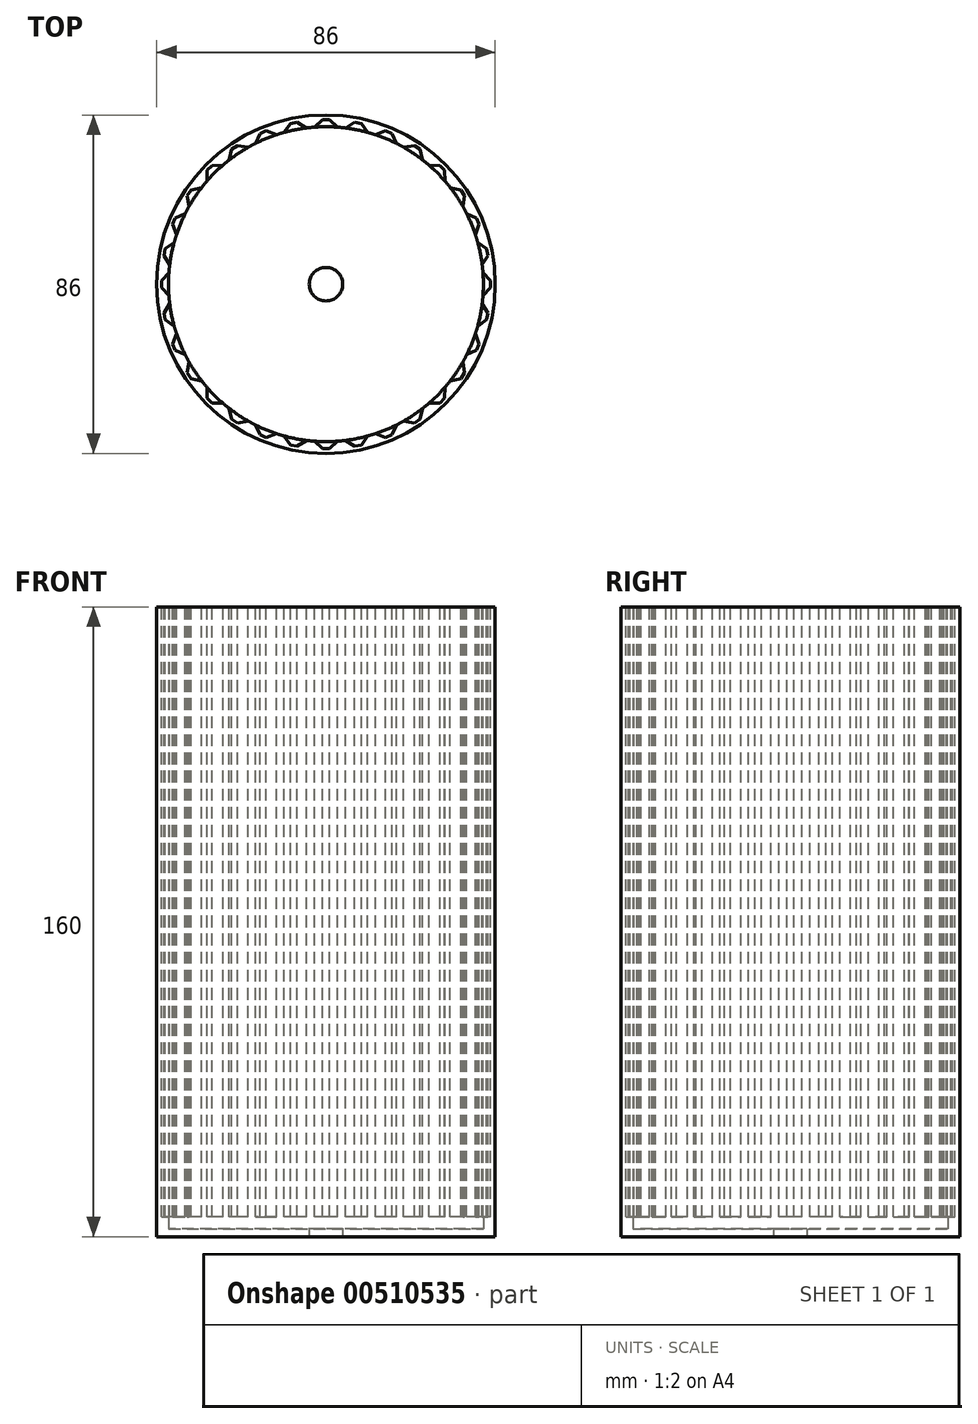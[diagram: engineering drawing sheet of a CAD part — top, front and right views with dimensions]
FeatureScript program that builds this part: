
annotation { "Feature Type Name" : "Feature", "Feature Type Description" : "" }
export const myFeature = defineFeature(function(context is Context, id is Id, definition is map)
    precondition{}
    {
        {
            var Q0;
            Q0=qCreatedBy(makeId("Top.planeOp"),FACE);
            var sketch = newSketch(context, id + "F0", { "sketchPlane" : qUnion([Q0])});
            skCircle(sketch, "E0", {"center": v(0, 0) * mm, "radius": 4.25 * mm});
            skCircle(sketch, "E1", {"center": v(0, 0) * mm, "radius": 40 * mm});
            skCircle(sketch, "E2", {"center": v(0, 0) * mm, "radius": 43 * mm});
            skSolve(sketch);
        }
        {
            var Q0;
            Q0=makeQuery(id+"F0.imprint","IMPRINT",FACE,{"disambiguationData":[TD([[makeQuery(id+"F0.imprint","IMPRINT",EDGE,{"derivedFrom":sQuery(id+"F0.wireOp",EDGE,"E0")}),-1.0]])]});
            var Q1;
            Q1=makeQuery(id+"F0.imprint","IMPRINT",FACE,{"disambiguationData":[TD([[makeQuery(id+"F0.imprint","IMPRINT",EDGE,{"derivedFrom":sQuery(id+"F0.wireOp",EDGE,"E1")}),-1.0]])]});
            extrude(context, id + "F1", {"entities" : qUnion([Q0, Q1]), "depth" : 2 * mm});
        }
        {
            var Q0;
            Q0=makeQuery(id+"F0.imprint","IMPRINT",FACE,{"disambiguationData":[TD([[makeQuery(id+"F0.imprint","IMPRINT",EDGE,{"derivedFrom":sQuery(id+"F0.wireOp",EDGE,"E1")}),-1.0]])]});
            extrude(context, id + "F2", {"entities" : qUnion([Q0]), "operationType" : NewBodyOperationType.ADD, "depth" : 160 * mm});
        }
        {
            var Q0;
            Q0=makeQuery(id+"F2.opExtrude","CAP_FACE",FACE,{"disambiguationData":[OSD([sQuery(id+"F0.wireOp",EDGE,"E1"),sQuery(id+"F0.wireOp",EDGE,"E2")])],"isStart":false});
            var sketch = newSketch(context, id + "F3", { "sketchPlane" : qUnion([Q0])});
            skLineSegment(sketch, "E3", {"start": v(-4.92, 50) * mm, "end": v(4.92, 50) * mm, "construction": true});
            skLineSegment(sketch, "E4", {"start": v(0, 0) * mm, "end": v(4.92, 50) * mm, "construction": true});
            skLineSegment(sketch, "E5", {"start": v(-3.84, 39) * mm, "end": v(-0.87, 41.8) * mm});
            skLineSegment(sketch, "E6", {"start": v(0.87, 41.8) * mm, "end": v(3.84, 39) * mm});
            skPoint(sketch, "E7.center", {"position": v(0, 0) * mm});
            skLineSegment(sketch, "E8", {"start": v(-0.87, 41.8) * mm, "end": v(0.87, 41.8) * mm});
            skPoint(sketch, "E9.orphan", {"position": v(0, 42.6) * mm});
            skLineSegment(sketch, "E10.1.0", {"start": v(-7.3, 41.16) * mm, "end": v(-3.84, 39) * mm});
            skLineSegment(sketch, "E10.1.1", {"start": v(-9, 40.82) * mm, "end": v(-7.3, 41.16) * mm});
            skLineSegment(sketch, "E10.1.2", {"start": v(-11.38, 37.5) * mm, "end": v(-9, 40.82) * mm});
            skPoint(sketch, "E10.1.3", {"position": v(-8.31, 41.79) * mm});
            skLineSegment(sketch, "E10.2.0", {"start": v(-15.19, 38.94) * mm, "end": v(-11.38, 37.5) * mm});
            skLineSegment(sketch, "E10.2.1", {"start": v(-16.8, 38.28) * mm, "end": v(-15.19, 38.94) * mm});
            skLineSegment(sketch, "E10.2.2", {"start": v(-18.47, 34.56) * mm, "end": v(-16.8, 38.28) * mm});
            skPoint(sketch, "E10.2.3", {"position": v(-16.3, 39.36) * mm});
            skLineSegment(sketch, "E10.3.0", {"start": v(-22.5, 35.23) * mm, "end": v(-18.47, 34.56) * mm});
            skLineSegment(sketch, "E10.3.1", {"start": v(-23.94, 34.27) * mm, "end": v(-22.5, 35.23) * mm});
            skLineSegment(sketch, "E10.3.2", {"start": v(-24.86, 30.3) * mm, "end": v(-23.94, 34.27) * mm});
            skPoint(sketch, "E10.3.3", {"position": v(-23.67, 35.43) * mm});
            skLineSegment(sketch, "E10.4.0", {"start": v(-28.94, 30.17) * mm, "end": v(-24.86, 30.3) * mm});
            skLineSegment(sketch, "E10.4.1", {"start": v(-30.17, 28.94) * mm, "end": v(-28.94, 30.17) * mm});
            skLineSegment(sketch, "E10.4.2", {"start": v(-30.3, 24.86) * mm, "end": v(-30.17, 28.94) * mm});
            skPoint(sketch, "E10.4.3", {"position": v(-30.13, 30.13) * mm});
            skLineSegment(sketch, "E10.5.0", {"start": v(-34.27, 23.94) * mm, "end": v(-30.3, 24.86) * mm});
            skLineSegment(sketch, "E10.5.1", {"start": v(-35.23, 22.5) * mm, "end": v(-34.27, 23.94) * mm});
            skLineSegment(sketch, "E10.5.2", {"start": v(-34.56, 18.47) * mm, "end": v(-35.23, 22.5) * mm});
            skPoint(sketch, "E10.5.3", {"position": v(-35.43, 23.67) * mm});
            skLineSegment(sketch, "E10.6.0", {"start": v(-38.28, 16.8) * mm, "end": v(-34.56, 18.47) * mm});
            skLineSegment(sketch, "E10.6.1", {"start": v(-38.94, 15.19) * mm, "end": v(-38.28, 16.8) * mm});
            skLineSegment(sketch, "E10.6.2", {"start": v(-37.5, 11.38) * mm, "end": v(-38.94, 15.19) * mm});
            skPoint(sketch, "E10.6.3", {"position": v(-39.36, 16.3) * mm});
            skLineSegment(sketch, "E10.7.0", {"start": v(-40.82, 9) * mm, "end": v(-37.5, 11.38) * mm});
            skLineSegment(sketch, "E10.7.1", {"start": v(-41.16, 7.3) * mm, "end": v(-40.82, 9) * mm});
            skLineSegment(sketch, "E10.7.2", {"start": v(-39, 3.84) * mm, "end": v(-41.16, 7.3) * mm});
            skPoint(sketch, "E10.7.3", {"position": v(-41.79, 8.31) * mm});
            skLineSegment(sketch, "E10.8.0", {"start": v(-41.8, 0.87) * mm, "end": v(-39, 3.84) * mm});
            skLineSegment(sketch, "E10.8.1", {"start": v(-41.8, -0.87) * mm, "end": v(-41.8, 0.87) * mm});
            skLineSegment(sketch, "E10.8.2", {"start": v(-39, -3.84) * mm, "end": v(-41.8, -0.87) * mm});
            skPoint(sketch, "E10.8.3", {"position": v(-42.6, 0) * mm});
            skLineSegment(sketch, "E10.9.0", {"start": v(-41.16, -7.3) * mm, "end": v(-39, -3.84) * mm});
            skLineSegment(sketch, "E10.9.1", {"start": v(-40.82, -9) * mm, "end": v(-41.16, -7.3) * mm});
            skLineSegment(sketch, "E10.9.2", {"start": v(-37.5, -11.38) * mm, "end": v(-40.82, -9) * mm});
            skPoint(sketch, "E10.9.3", {"position": v(-41.79, -8.31) * mm});
            skLineSegment(sketch, "E10.10.0", {"start": v(-38.94, -15.19) * mm, "end": v(-37.5, -11.38) * mm});
            skLineSegment(sketch, "E10.10.1", {"start": v(-38.28, -16.8) * mm, "end": v(-38.94, -15.19) * mm});
            skLineSegment(sketch, "E10.10.2", {"start": v(-34.56, -18.47) * mm, "end": v(-38.28, -16.8) * mm});
            skPoint(sketch, "E10.10.3", {"position": v(-39.36, -16.3) * mm});
            skLineSegment(sketch, "E10.11.0", {"start": v(-35.23, -22.5) * mm, "end": v(-34.56, -18.47) * mm});
            skLineSegment(sketch, "E10.11.1", {"start": v(-34.27, -23.94) * mm, "end": v(-35.23, -22.5) * mm});
            skLineSegment(sketch, "E10.11.2", {"start": v(-30.3, -24.86) * mm, "end": v(-34.27, -23.94) * mm});
            skPoint(sketch, "E10.11.3", {"position": v(-35.43, -23.67) * mm});
            skLineSegment(sketch, "E10.12.0", {"start": v(-30.17, -28.94) * mm, "end": v(-30.3, -24.86) * mm});
            skLineSegment(sketch, "E10.12.1", {"start": v(-28.94, -30.17) * mm, "end": v(-30.17, -28.94) * mm});
            skLineSegment(sketch, "E10.12.2", {"start": v(-24.86, -30.3) * mm, "end": v(-28.94, -30.17) * mm});
            skPoint(sketch, "E10.12.3", {"position": v(-30.13, -30.13) * mm});
            skLineSegment(sketch, "E10.13.0", {"start": v(-23.94, -34.27) * mm, "end": v(-24.86, -30.3) * mm});
            skLineSegment(sketch, "E10.13.1", {"start": v(-22.5, -35.23) * mm, "end": v(-23.94, -34.27) * mm});
            skLineSegment(sketch, "E10.13.2", {"start": v(-18.47, -34.56) * mm, "end": v(-22.5, -35.23) * mm});
            skPoint(sketch, "E10.13.3", {"position": v(-23.67, -35.43) * mm});
            skLineSegment(sketch, "E10.14.0", {"start": v(-16.8, -38.28) * mm, "end": v(-18.47, -34.56) * mm});
            skLineSegment(sketch, "E10.14.1", {"start": v(-15.19, -38.94) * mm, "end": v(-16.8, -38.28) * mm});
            skLineSegment(sketch, "E10.14.2", {"start": v(-11.38, -37.5) * mm, "end": v(-15.19, -38.94) * mm});
            skPoint(sketch, "E10.14.3", {"position": v(-16.3, -39.36) * mm});
            skLineSegment(sketch, "E10.15.0", {"start": v(-9, -40.82) * mm, "end": v(-11.38, -37.5) * mm});
            skLineSegment(sketch, "E10.15.1", {"start": v(-7.3, -41.16) * mm, "end": v(-9, -40.82) * mm});
            skLineSegment(sketch, "E10.15.2", {"start": v(-3.84, -39) * mm, "end": v(-7.3, -41.16) * mm});
            skPoint(sketch, "E10.15.3", {"position": v(-8.31, -41.79) * mm});
            skLineSegment(sketch, "E10.16.0", {"start": v(-0.87, -41.8) * mm, "end": v(-3.84, -39) * mm});
            skLineSegment(sketch, "E10.16.1", {"start": v(0.87, -41.8) * mm, "end": v(-0.87, -41.8) * mm});
            skLineSegment(sketch, "E10.16.2", {"start": v(3.84, -39) * mm, "end": v(0.87, -41.8) * mm});
            skPoint(sketch, "E10.16.3", {"position": v(0, -42.6) * mm});
            skLineSegment(sketch, "E10.17.0", {"start": v(7.3, -41.16) * mm, "end": v(3.84, -39) * mm});
            skLineSegment(sketch, "E10.17.1", {"start": v(9, -40.82) * mm, "end": v(7.3, -41.16) * mm});
            skLineSegment(sketch, "E10.17.2", {"start": v(11.38, -37.5) * mm, "end": v(9, -40.82) * mm});
            skPoint(sketch, "E10.17.3", {"position": v(8.31, -41.79) * mm});
            skLineSegment(sketch, "E10.18.0", {"start": v(15.19, -38.94) * mm, "end": v(11.38, -37.5) * mm});
            skLineSegment(sketch, "E10.18.1", {"start": v(16.8, -38.28) * mm, "end": v(15.19, -38.94) * mm});
            skLineSegment(sketch, "E10.18.2", {"start": v(18.47, -34.56) * mm, "end": v(16.8, -38.28) * mm});
            skPoint(sketch, "E10.18.3", {"position": v(16.3, -39.36) * mm});
            skLineSegment(sketch, "E10.19.0", {"start": v(22.5, -35.23) * mm, "end": v(18.47, -34.56) * mm});
            skLineSegment(sketch, "E10.19.1", {"start": v(23.94, -34.27) * mm, "end": v(22.5, -35.23) * mm});
            skLineSegment(sketch, "E10.19.2", {"start": v(24.86, -30.3) * mm, "end": v(23.94, -34.27) * mm});
            skPoint(sketch, "E10.19.3", {"position": v(23.67, -35.43) * mm});
            skLineSegment(sketch, "E10.20.0", {"start": v(28.94, -30.17) * mm, "end": v(24.86, -30.3) * mm});
            skLineSegment(sketch, "E10.20.1", {"start": v(30.17, -28.94) * mm, "end": v(28.94, -30.17) * mm});
            skLineSegment(sketch, "E10.20.2", {"start": v(30.3, -24.86) * mm, "end": v(30.17, -28.94) * mm});
            skPoint(sketch, "E10.20.3", {"position": v(30.13, -30.13) * mm});
            skLineSegment(sketch, "E10.21.0", {"start": v(34.27, -23.94) * mm, "end": v(30.3, -24.86) * mm});
            skLineSegment(sketch, "E10.21.1", {"start": v(35.23, -22.5) * mm, "end": v(34.27, -23.94) * mm});
            skLineSegment(sketch, "E10.21.2", {"start": v(34.56, -18.47) * mm, "end": v(35.23, -22.5) * mm});
            skPoint(sketch, "E10.21.3", {"position": v(35.43, -23.67) * mm});
            skLineSegment(sketch, "E10.22.0", {"start": v(38.28, -16.8) * mm, "end": v(34.56, -18.47) * mm});
            skLineSegment(sketch, "E10.22.1", {"start": v(38.94, -15.19) * mm, "end": v(38.28, -16.8) * mm});
            skLineSegment(sketch, "E10.22.2", {"start": v(37.5, -11.38) * mm, "end": v(38.94, -15.19) * mm});
            skPoint(sketch, "E10.22.3", {"position": v(39.36, -16.3) * mm});
            skLineSegment(sketch, "E10.23.0", {"start": v(40.82, -9) * mm, "end": v(37.5, -11.38) * mm});
            skLineSegment(sketch, "E10.23.1", {"start": v(41.16, -7.3) * mm, "end": v(40.82, -9) * mm});
            skLineSegment(sketch, "E10.23.2", {"start": v(39, -3.84) * mm, "end": v(41.16, -7.3) * mm});
            skPoint(sketch, "E10.23.3", {"position": v(41.79, -8.31) * mm});
            skLineSegment(sketch, "E10.24.0", {"start": v(41.8, -0.87) * mm, "end": v(39, -3.84) * mm});
            skLineSegment(sketch, "E10.24.1", {"start": v(41.8, 0.87) * mm, "end": v(41.8, -0.87) * mm});
            skLineSegment(sketch, "E10.24.2", {"start": v(39, 3.84) * mm, "end": v(41.8, 0.87) * mm});
            skPoint(sketch, "E10.24.3", {"position": v(42.6, 0) * mm});
            skLineSegment(sketch, "E10.25.0", {"start": v(41.16, 7.3) * mm, "end": v(39, 3.84) * mm});
            skLineSegment(sketch, "E10.25.1", {"start": v(40.82, 9) * mm, "end": v(41.16, 7.3) * mm});
            skLineSegment(sketch, "E10.25.2", {"start": v(37.5, 11.38) * mm, "end": v(40.82, 9) * mm});
            skPoint(sketch, "E10.25.3", {"position": v(41.79, 8.31) * mm});
            skLineSegment(sketch, "E10.26.0", {"start": v(38.94, 15.19) * mm, "end": v(37.5, 11.38) * mm});
            skLineSegment(sketch, "E10.26.1", {"start": v(38.28, 16.8) * mm, "end": v(38.94, 15.19) * mm});
            skLineSegment(sketch, "E10.26.2", {"start": v(34.56, 18.47) * mm, "end": v(38.28, 16.8) * mm});
            skPoint(sketch, "E10.26.3", {"position": v(39.36, 16.3) * mm});
            skLineSegment(sketch, "E10.27.0", {"start": v(35.23, 22.5) * mm, "end": v(34.56, 18.47) * mm});
            skLineSegment(sketch, "E10.27.1", {"start": v(34.27, 23.94) * mm, "end": v(35.23, 22.5) * mm});
            skLineSegment(sketch, "E10.27.2", {"start": v(30.3, 24.86) * mm, "end": v(34.27, 23.94) * mm});
            skPoint(sketch, "E10.27.3", {"position": v(35.43, 23.67) * mm});
            skLineSegment(sketch, "E10.28.0", {"start": v(30.17, 28.94) * mm, "end": v(30.3, 24.86) * mm});
            skLineSegment(sketch, "E10.28.1", {"start": v(28.94, 30.17) * mm, "end": v(30.17, 28.94) * mm});
            skLineSegment(sketch, "E10.28.2", {"start": v(24.86, 30.3) * mm, "end": v(28.94, 30.17) * mm});
            skPoint(sketch, "E10.28.3", {"position": v(30.13, 30.13) * mm});
            skLineSegment(sketch, "E10.29.0", {"start": v(23.94, 34.27) * mm, "end": v(24.86, 30.3) * mm});
            skLineSegment(sketch, "E10.29.1", {"start": v(22.5, 35.23) * mm, "end": v(23.94, 34.27) * mm});
            skLineSegment(sketch, "E10.29.2", {"start": v(18.47, 34.56) * mm, "end": v(22.5, 35.23) * mm});
            skPoint(sketch, "E10.29.3", {"position": v(23.67, 35.43) * mm});
            skLineSegment(sketch, "E10.30.0", {"start": v(16.8, 38.28) * mm, "end": v(18.47, 34.56) * mm});
            skLineSegment(sketch, "E10.30.1", {"start": v(15.19, 38.94) * mm, "end": v(16.8, 38.28) * mm});
            skLineSegment(sketch, "E10.30.2", {"start": v(11.38, 37.5) * mm, "end": v(15.19, 38.94) * mm});
            skPoint(sketch, "E10.30.3", {"position": v(16.3, 39.36) * mm});
            skLineSegment(sketch, "E10.31.0", {"start": v(9, 40.82) * mm, "end": v(11.38, 37.5) * mm});
            skLineSegment(sketch, "E10.31.1", {"start": v(7.3, 41.16) * mm, "end": v(9, 40.82) * mm});
            skLineSegment(sketch, "E10.31.2", {"start": v(3.84, 39) * mm, "end": v(7.3, 41.16) * mm});
            skPoint(sketch, "E10.31.3", {"position": v(8.31, 41.79) * mm});
            skSolve(sketch);
        }
        {
            var Q0;
            {var subQ0=sQuery(id+"F3.wireOp",EDGE,"E10.2.1");Q0=makeQuery(id+"F3.imprint","IMPRINT",FACE,{"disambiguationData":[TD([[makeQuery(id+"F3.imprint","IMPRINT",EDGE,{"derivedFrom":subQ0}),-1.0]])]});}
            var Q1;
            {var subQ0=sQuery(id+"F3.wireOp",EDGE,"E10.1.1");Q1=makeQuery(id+"F3.imprint","IMPRINT",FACE,{"disambiguationData":[TD([[makeQuery(id+"F3.imprint","IMPRINT",EDGE,{"derivedFrom":subQ0}),-1.0]])]});}
            var Q2;
            {var subQ0=sQuery(id+"F3.wireOp",EDGE,"E8");Q2=makeQuery(id+"F3.imprint","IMPRINT",FACE,{"disambiguationData":[TD([[makeQuery(id+"F3.imprint","IMPRINT",EDGE,{"derivedFrom":subQ0}),-1.0]])]});}
            var Q3;
            {var subQ0=sQuery(id+"F3.wireOp",EDGE,"E10.31.1");Q3=makeQuery(id+"F3.imprint","IMPRINT",FACE,{"disambiguationData":[TD([[makeQuery(id+"F3.imprint","IMPRINT",EDGE,{"derivedFrom":subQ0}),-1.0]])]});}
            var Q4;
            {var subQ0=sQuery(id+"F3.wireOp",EDGE,"E10.30.1");Q4=makeQuery(id+"F3.imprint","IMPRINT",FACE,{"disambiguationData":[TD([[makeQuery(id+"F3.imprint","IMPRINT",EDGE,{"derivedFrom":subQ0}),-1.0]])]});}
            var Q5;
            {var subQ0=sQuery(id+"F3.wireOp",EDGE,"E10.3.1");Q5=makeQuery(id+"F3.imprint","IMPRINT",FACE,{"disambiguationData":[TD([[makeQuery(id+"F3.imprint","IMPRINT",EDGE,{"derivedFrom":subQ0}),-1.0]])]});}
            var Q6;
            {var subQ0=sQuery(id+"F3.wireOp",EDGE,"E10.4.1");Q6=makeQuery(id+"F3.imprint","IMPRINT",FACE,{"disambiguationData":[TD([[makeQuery(id+"F3.imprint","IMPRINT",EDGE,{"derivedFrom":subQ0}),-1.0]])]});}
            var Q7;
            {var subQ0=sQuery(id+"F3.wireOp",EDGE,"E10.5.1");Q7=makeQuery(id+"F3.imprint","IMPRINT",FACE,{"disambiguationData":[TD([[makeQuery(id+"F3.imprint","IMPRINT",EDGE,{"derivedFrom":subQ0}),-1.0]])]});}
            var Q8;
            {var subQ0=sQuery(id+"F3.wireOp",EDGE,"E10.6.1");Q8=makeQuery(id+"F3.imprint","IMPRINT",FACE,{"disambiguationData":[TD([[makeQuery(id+"F3.imprint","IMPRINT",EDGE,{"derivedFrom":subQ0}),-1.0]])]});}
            var Q9;
            {var subQ0=sQuery(id+"F3.wireOp",EDGE,"E10.7.1");Q9=makeQuery(id+"F3.imprint","IMPRINT",FACE,{"disambiguationData":[TD([[makeQuery(id+"F3.imprint","IMPRINT",EDGE,{"derivedFrom":subQ0}),-1.0]])]});}
            var Q10;
            {var subQ0=sQuery(id+"F3.wireOp",EDGE,"E10.29.1");Q10=makeQuery(id+"F3.imprint","IMPRINT",FACE,{"disambiguationData":[TD([[makeQuery(id+"F3.imprint","IMPRINT",EDGE,{"derivedFrom":subQ0}),-1.0]])]});}
            var Q11;
            {var subQ0=sQuery(id+"F3.wireOp",EDGE,"E10.28.1");Q11=makeQuery(id+"F3.imprint","IMPRINT",FACE,{"disambiguationData":[TD([[makeQuery(id+"F3.imprint","IMPRINT",EDGE,{"derivedFrom":subQ0}),-1.0]])]});}
            var Q12;
            {var subQ0=sQuery(id+"F3.wireOp",EDGE,"E10.27.1");Q12=makeQuery(id+"F3.imprint","IMPRINT",FACE,{"disambiguationData":[TD([[makeQuery(id+"F3.imprint","IMPRINT",EDGE,{"derivedFrom":subQ0}),-1.0]])]});}
            var Q13;
            {var subQ0=sQuery(id+"F3.wireOp",EDGE,"E10.26.1");Q13=makeQuery(id+"F3.imprint","IMPRINT",FACE,{"disambiguationData":[TD([[makeQuery(id+"F3.imprint","IMPRINT",EDGE,{"derivedFrom":subQ0}),-1.0]])]});}
            var Q14;
            {var subQ0=sQuery(id+"F3.wireOp",EDGE,"E10.8.1");Q14=makeQuery(id+"F3.imprint","IMPRINT",FACE,{"disambiguationData":[TD([[makeQuery(id+"F3.imprint","IMPRINT",EDGE,{"derivedFrom":subQ0}),-1.0]])]});}
            var Q15;
            {var subQ0=sQuery(id+"F3.wireOp",EDGE,"E10.9.1");Q15=makeQuery(id+"F3.imprint","IMPRINT",FACE,{"disambiguationData":[TD([[makeQuery(id+"F3.imprint","IMPRINT",EDGE,{"derivedFrom":subQ0}),-1.0]])]});}
            var Q16;
            {var subQ0=sQuery(id+"F3.wireOp",EDGE,"E10.10.1");Q16=makeQuery(id+"F3.imprint","IMPRINT",FACE,{"disambiguationData":[TD([[makeQuery(id+"F3.imprint","IMPRINT",EDGE,{"derivedFrom":subQ0}),-1.0]])]});}
            var Q17;
            {var subQ0=sQuery(id+"F3.wireOp",EDGE,"E10.11.1");Q17=makeQuery(id+"F3.imprint","IMPRINT",FACE,{"disambiguationData":[TD([[makeQuery(id+"F3.imprint","IMPRINT",EDGE,{"derivedFrom":subQ0}),-1.0]])]});}
            var Q18;
            {var subQ0=sQuery(id+"F3.wireOp",EDGE,"E10.12.1");Q18=makeQuery(id+"F3.imprint","IMPRINT",FACE,{"disambiguationData":[TD([[makeQuery(id+"F3.imprint","IMPRINT",EDGE,{"derivedFrom":subQ0}),-1.0]])]});}
            var Q19;
            {var subQ0=sQuery(id+"F3.wireOp",EDGE,"E10.13.1");Q19=makeQuery(id+"F3.imprint","IMPRINT",FACE,{"disambiguationData":[TD([[makeQuery(id+"F3.imprint","IMPRINT",EDGE,{"derivedFrom":subQ0}),-1.0]])]});}
            var Q20;
            {var subQ0=sQuery(id+"F3.wireOp",EDGE,"E10.14.1");Q20=makeQuery(id+"F3.imprint","IMPRINT",FACE,{"disambiguationData":[TD([[makeQuery(id+"F3.imprint","IMPRINT",EDGE,{"derivedFrom":subQ0}),-1.0]])]});}
            var Q21;
            {var subQ0=sQuery(id+"F3.wireOp",EDGE,"E10.15.1");Q21=makeQuery(id+"F3.imprint","IMPRINT",FACE,{"disambiguationData":[TD([[makeQuery(id+"F3.imprint","IMPRINT",EDGE,{"derivedFrom":subQ0}),-1.0]])]});}
            var Q22;
            {var subQ0=sQuery(id+"F3.wireOp",EDGE,"E10.16.1");Q22=makeQuery(id+"F3.imprint","IMPRINT",FACE,{"disambiguationData":[TD([[makeQuery(id+"F3.imprint","IMPRINT",EDGE,{"derivedFrom":subQ0}),-1.0]])]});}
            var Q23;
            {var subQ0=sQuery(id+"F3.wireOp",EDGE,"E10.17.1");Q23=makeQuery(id+"F3.imprint","IMPRINT",FACE,{"disambiguationData":[TD([[makeQuery(id+"F3.imprint","IMPRINT",EDGE,{"derivedFrom":subQ0}),-1.0]])]});}
            var Q24;
            {var subQ0=sQuery(id+"F3.wireOp",EDGE,"E10.18.1");Q24=makeQuery(id+"F3.imprint","IMPRINT",FACE,{"disambiguationData":[TD([[makeQuery(id+"F3.imprint","IMPRINT",EDGE,{"derivedFrom":subQ0}),-1.0]])]});}
            var Q25;
            {var subQ0=sQuery(id+"F3.wireOp",EDGE,"E10.25.1");Q25=makeQuery(id+"F3.imprint","IMPRINT",FACE,{"disambiguationData":[TD([[makeQuery(id+"F3.imprint","IMPRINT",EDGE,{"derivedFrom":subQ0}),-1.0]])]});}
            var Q26;
            {var subQ0=sQuery(id+"F3.wireOp",EDGE,"E10.24.1");Q26=makeQuery(id+"F3.imprint","IMPRINT",FACE,{"disambiguationData":[TD([[makeQuery(id+"F3.imprint","IMPRINT",EDGE,{"derivedFrom":subQ0}),-1.0]])]});}
            var Q27;
            {var subQ0=sQuery(id+"F3.wireOp",EDGE,"E10.23.1");Q27=makeQuery(id+"F3.imprint","IMPRINT",FACE,{"disambiguationData":[TD([[makeQuery(id+"F3.imprint","IMPRINT",EDGE,{"derivedFrom":subQ0}),-1.0]])]});}
            var Q28;
            {var subQ0=sQuery(id+"F3.wireOp",EDGE,"E10.22.1");Q28=makeQuery(id+"F3.imprint","IMPRINT",FACE,{"disambiguationData":[TD([[makeQuery(id+"F3.imprint","IMPRINT",EDGE,{"derivedFrom":subQ0}),-1.0]])]});}
            var Q29;
            {var subQ0=sQuery(id+"F3.wireOp",EDGE,"E10.21.1");Q29=makeQuery(id+"F3.imprint","IMPRINT",FACE,{"disambiguationData":[TD([[makeQuery(id+"F3.imprint","IMPRINT",EDGE,{"derivedFrom":subQ0}),-1.0]])]});}
            var Q30;
            {var subQ0=sQuery(id+"F3.wireOp",EDGE,"E10.20.1");Q30=makeQuery(id+"F3.imprint","IMPRINT",FACE,{"disambiguationData":[TD([[makeQuery(id+"F3.imprint","IMPRINT",EDGE,{"derivedFrom":subQ0}),-1.0]])]});}
            var Q31;
            {var subQ0=sQuery(id+"F3.wireOp",EDGE,"E10.19.1");Q31=makeQuery(id+"F3.imprint","IMPRINT",FACE,{"disambiguationData":[TD([[makeQuery(id+"F3.imprint","IMPRINT",EDGE,{"derivedFrom":subQ0}),-1.0]])]});}
            extrude(context, id + "F4", {"entities" : qUnion([Q0, Q1, Q2, Q3, Q4, Q5, Q6, Q7, Q8, Q9, Q10, Q11, Q12, Q13, Q14, Q15, Q16, Q17, Q18, Q19, Q20, Q21, Q22, Q23, Q24, Q25, Q26, Q27, Q28, Q29, Q30, Q31]), "operationType" : NewBodyOperationType.REMOVE, "oppositeDirection" : true, "depth" : 155 * mm});
        }
    });
